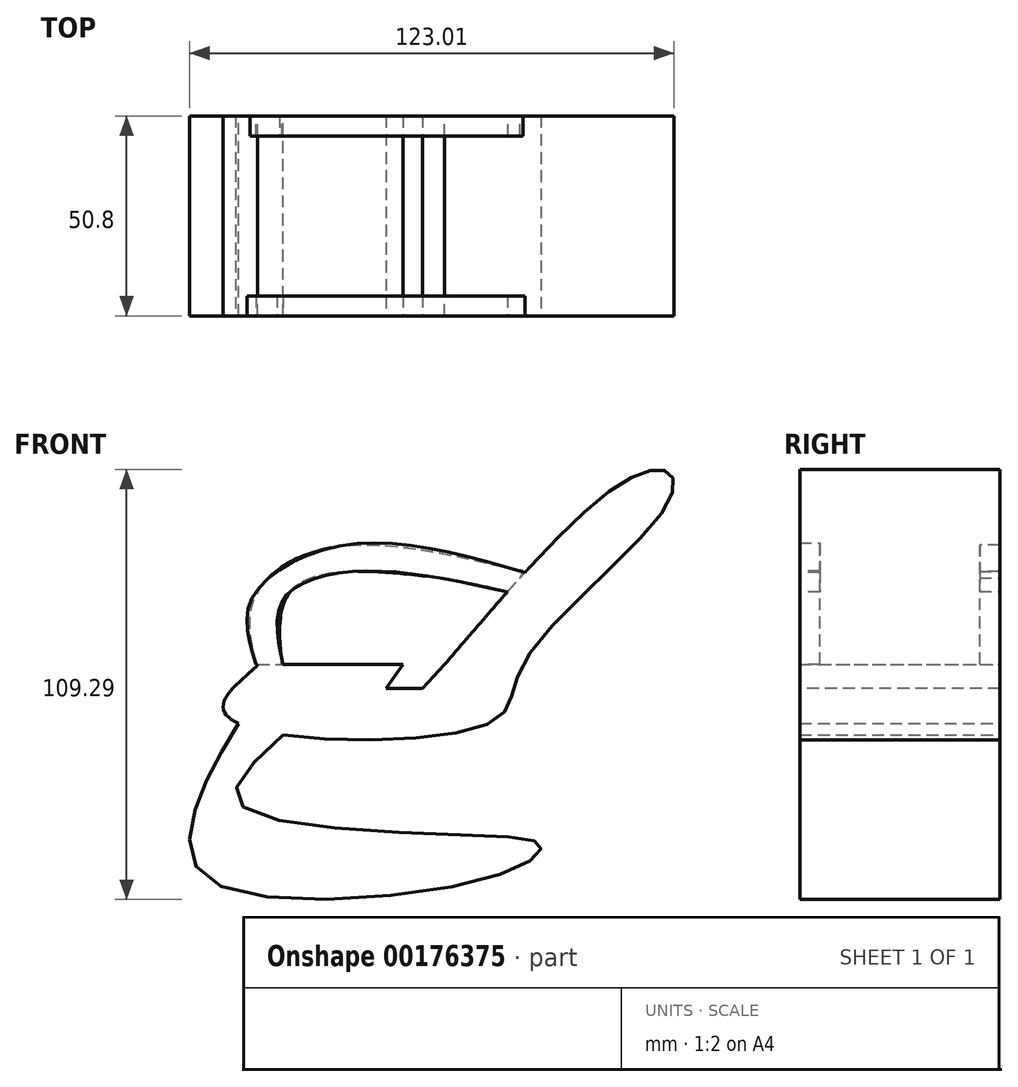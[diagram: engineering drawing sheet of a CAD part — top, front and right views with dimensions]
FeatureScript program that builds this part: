
annotation { "Feature Type Name" : "Feature", "Feature Type Description" : "" }
export const myFeature = defineFeature(function(context is Context, id is Id, definition is map)
    precondition{}
    {
        {
            var Q0;
            Q0=qCreatedBy(makeId("Front.planeOp"),FACE);
            var sketch = newSketch(context, id + "F0", { "sketchPlane" : qUnion([Q0])});
            skFitSpline(sketch, "E0", {"points": [v(-19.86, 0) * mm, v(25.04, 46.05) * mm, v(36.84, 48.93) * mm, v(36.84, 40.87) * mm, v(0, 0) * mm, v(-6.9, -14.1) * mm, v(-68.2, -16.4) * mm, v(-75.7, -8.92) * mm, v(-67.35, 0) * mm, v(-68.5, 0) * mm], "startDerivative": vector(254.86, 298.07) * mm, "endDerivative": vector(-68.06, -13.8) * mm});
            skFitSpline(sketch, "E1", {"points": [v(-60.95, -17.83) * mm, v(-71.95, -35.4) * mm, v(-4.6, -43.75) * mm, v(4.6, -46.34) * mm, v(-5.47, -53.24) * mm, v(-78.86, -55.26) * mm, v(-83.46, -37.7) * mm, v(-72.22, -15) * mm], "startDerivative": vector(-181.4, -163.68) * mm, "endDerivative": vector(99.6, 164.24) * mm});
            skLineSegment(sketch, "E2", {"start": v(-67.35, 0) * mm, "end": v(-19.86, 0) * mm});
            skFitSpline(sketch, "E3", {"points": [v(-59.58, 0) * mm, v(-55.83, 12.95) * mm, v(-45.76, 19) * mm, v(-3.4, 19.26) * mm], "startDerivative": vector(9.08, 53.39) * mm, "endDerivative": vector(103.02, -5.49) * mm});
            skFitSpline(sketch, "E4", {"points": [v(-67.9, 0.12) * mm, v(-63.9, 13.24) * mm, v(-50.37, 24.46) * mm, v(1.37, 24.29) * mm, v(1.78, 24.74) * mm], "startDerivative": vector(14.67, 57.12) * mm, "endDerivative": vector(1.47, 10.21) * mm});
            skSolve(sketch);
        }
        {
            var Q0;
            {var subQ0=sQuery(id+"F0.wireOp",EDGE,"E4");var subQ1=sQuery(id+"F0.wireOp",EDGE,"E0");var subQ2=makeQuery(id+"F0.imprint","INTERSECT",VERTEX,{"disambiguationData":[OD(0.0)],"derivedFrom":[subQ1,subQ0]});Q0=makeQuery(id+"F0.imprint","IMPRINT",FACE,{"disambiguationData":[TD([[makeQuery(id+"F0.imprint","IMPRINT",EDGE,{"disambiguationData":[TD([[subQ2,1.0]])],"derivedFrom":subQ1}),-1.0]])]});}
            var Q1;
            {var subQ0=sQuery(id+"F0.wireOp",EDGE,"E1");Q1=makeQuery(id+"F0.imprint","IMPRINT",FACE,{"disambiguationData":[TD([[makeQuery(id+"F0.imprint","IMPRINT",EDGE,{"derivedFrom":subQ0}),-1.0]])]});}
            var Q2;
            {var subQ3=sQuery(id+"F0.wireOp",EDGE,"E2");var subQ10=makeQuery(id+"F0.imprint","IMPRINT",VERTEX,{"derivedFrom":subQ3});Q2=makeQuery(id+"F0.imprint","IMPRINT",FACE,{"disambiguationData":[TD([[makeQuery(id+"F0.imprint","IMPRINT",EDGE,{"disambiguationData":[TD([[subQ10,1.0]])],"derivedFrom":subQ3}),-1.0]])]});}
            extrude(context, id + "F1", {"entities" : qUnion([Q0, Q1, Q2]), "depth" : 50.8 * mm});
        }
        {
            var Q0;
            Q0=makeQuery(id+"F1.opExtrude","CAP_FACE",FACE,{"disambiguationData":[OSD([sQuery(id+"F0.wireOp",EDGE,"E0"),sQuery(id+"F0.wireOp",EDGE,"E1"),sQuery(id+"F0.wireOp",EDGE,"E2")])],"isStart":false});
            var sketch = newSketch(context, id + "F2", { "sketchPlane" : qUnion([Q0])});
            skLineSegment(sketch, "E5", {"start": v(-19.86, 0) * mm, "end": v(-25.51, -6.04) * mm});
            skLineSegment(sketch, "E6", {"start": v(-25.51, -6.04) * mm, "end": v(-34.72, -6.04) * mm});
            skLineSegment(sketch, "E7", {"start": v(-34.72, -6.04) * mm, "end": v(-30.4, 0) * mm});
            skLineSegment(sketch, "E8", {"start": v(-30.4, 0) * mm, "end": v(-19.86, 0) * mm});
            skSolve(sketch);
        }
        {
            var Q0;
            Q0=makeQuery(id+"F2.imprint","IMPRINT",FACE,{"disambiguationData":[TD([[makeQuery(id+"F2.imprint","IMPRINT",EDGE,{"derivedFrom":sQuery(id+"F2.wireOp",EDGE,"E5")}),-1.0]])]});
            extrude(context, id + "F3", {"entities" : qUnion([Q0]), "operationType" : NewBodyOperationType.REMOVE, "oppositeDirection" : true, "depth" : 50.8 * mm});
        }
        {
            var Q0;
            Q0=qCreatedBy(makeId("Front.planeOp"),FACE);
            var sketch = newSketch(context, id + "F4", { "sketchPlane" : qUnion([Q0])});
            skFitSpline(sketch, "E9", {"points": [v(-61.2, 0) * mm, v(-60.62, 15.83) * mm, v(-45.37, 23.6) * mm, v(-2.77, 18.13) * mm, v(-2.77, 17.84) * mm, v(-2.77, 17.56) * mm], "startDerivative": vector(-6.82, 68.58) * mm, "endDerivative": vector(1.26, -8.62) * mm});
            skFitSpline(sketch, "E10", {"points": [v(-67.82, 0) * mm, v(-68.1, 16.98) * mm, v(-48.82, 29.64) * mm, v(0, 23.6) * mm], "startDerivative": vector(-14.68, 68.68) * mm, "endDerivative": vector(120.18, -29.24) * mm});
            skLineSegment(sketch, "E11", {"start": v(-67.82, 0) * mm, "end": v(-61.2, 0) * mm});
            skLineSegment(sketch, "E12", {"start": v(0, 23.6) * mm, "end": v(-2.77, 17.56) * mm});
            skSolve(sketch);
        }
        {
            var Q0;
            Q0=makeQuery(id+"F4.imprint","IMPRINT",FACE,{"disambiguationData":[TD([[makeQuery(id+"F4.imprint","IMPRINT",EDGE,{"derivedFrom":sQuery(id+"F4.wireOp",EDGE,"E9")}),1.0]])]});
            extrude(context, id + "F5", {"entities" : qUnion([Q0]), "operationType" : NewBodyOperationType.ADD, "depth" : 5.08 * mm});
        }
        {
            var Q0;
            Q0=qCreatedBy(makeId("Front.planeOp"),FACE);
            cPlane(context, id + "F6", {"entities" : qUnion([Q0]), "cplaneType" : CPlaneType.OFFSET, "offset" : 50.8 * mm, "width" : 152.4 * mm, "height" : 152.4 * mm});
        }
        {
            var Q0;
            Q0=qCreatedBy(id+"F6.planeOp",FACE);
            var sketch = newSketch(context, id + "F7", { "sketchPlane" : qUnion([Q0])});
            skLineSegment(sketch, "E13", {"start": v(-67.82, 0) * mm, "end": v(-60.91, 0) * mm});
            skPoint(sketch, "E14.startSnap0", {"position": v(-2.4, 21.3) * mm});
            skFitSpline(sketch, "E15", {"points": [v(-60.91, 0) * mm, v(-60.91, 16.35) * mm, v(-41.83, 23.69) * mm, v(-3.12, 18.26) * mm], "startDerivative": vector(-14.1, 66.96) * mm, "endDerivative": vector(95.65, -21.3) * mm});
            skFitSpline(sketch, "E16", {"points": [v(-67.82, 0) * mm, v(-69, 16.35) * mm, v(-45.22, 30.34) * mm, v(0.96, 23.28) * mm], "startDerivative": vector(-20.88, 67.31) * mm, "endDerivative": vector(113.26, -32.76) * mm});
            skLineSegment(sketch, "E17", {"start": v(0.96, 23.28) * mm, "end": v(-3.12, 18.26) * mm});
            skSolve(sketch);
        }
        {
            var Q0;
            Q0=makeQuery(id+"F7.imprint","IMPRINT",FACE,{"disambiguationData":[TD([[makeQuery(id+"F7.imprint","IMPRINT",EDGE,{"derivedFrom":sQuery(id+"F7.wireOp",EDGE,"E13")}),1.0]])]});
            extrude(context, id + "F8", {"entities" : qUnion([Q0]), "operationType" : NewBodyOperationType.ADD, "oppositeDirection" : true, "depth" : 5.08 * mm});
        }
    });
